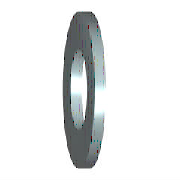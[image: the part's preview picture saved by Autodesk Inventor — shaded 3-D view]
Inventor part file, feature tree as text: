
AUTODESK INVENTOR PART (.ipt)
format: ipt  version: 2025 (Build 290162010, 162A)  size: 105,984 bytes
history: native  units: mm (DEFAULTED — no unit token found)
features: other x1, plane x1
ambient origin geometry x7: Origin, YZ Plane, XY Plane, X Axis, Y Axis, Z Axis, Center Point
bodies: Solid1 (feature_tree), Body (feature_tree)
feature tree (2):
  other  "Work Axis1"
  plane  "Work Plane1"
